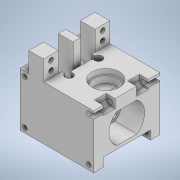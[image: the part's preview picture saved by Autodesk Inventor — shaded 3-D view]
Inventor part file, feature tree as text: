
AUTODESK INVENTOR PART (.ipt)
format: ipt  version: 2020 (Build 240168000, 168)  size: 453,120 bytes
history: native  units: mm
features: extrude x16, sketch x6, other x3
ambient origin geometry x8: Origin, YZ Plane, XZ Plane, XY Plane, X Axis, Y Axis, Z Axis, Center Point
bodies: Body1 (feature_tree)
feature tree (25):
  other  "Bryła1"
  extrude  "Wyciągnięcie proste1"  Depth=90.0mm
  sketch  "Szkic2"
  other  "Płaszczyzna konstrukcyjna1"
  extrude  "Wyciągnięcie proste2"  Depth=100.0mm
  extrude  "Wyciągnięcie proste3"  Depth=73.0mm TaperAngle=0.0deg
  sketch  "Szkic3"
  extrude  "Wyciągnięcie proste4"  Depth=6.5mm
  extrude  "Wyciągnięcie proste5"  Depth=6.5mm
  extrude  "Wyciągnięcie proste6"  Depth=6.5mm
  extrude  "Wyciągnięcie proste7"  Depth=6.5mm
  sketch  "Szkic4"
  extrude  "Wyciągnięcie proste8"  Depth=6.5mm
  extrude  "Wyciągnięcie proste9"  Depth=6.5mm
  extrude  "Wyciągnięcie proste10"  Depth=11.0mm
  extrude  "Wyciągnięcie proste11"  [1 undecoded]
  extrude  "Wyciągnięcie proste12"  Depth=64.0mm TaperAngle=0.0deg
  other  "Płaszczyzna konstrukcyjna2"
  extrude  "Wyciągnięcie proste13"  TaperAngle=0.0deg  [1 undecoded]
  extrude  "Wyciągnięcie proste14"  Depth=36.5mm
  extrude  "Wyciągnięcie proste15"  Depth=45.0mm
  extrude  "Wyciągnięcie proste16"  Depth=28.5mm
  sketch  "Szkic1"
  sketch  "Szkic5"
  sketch  "Szkic6"
note: 2 required parameter values undecoded (feature->parameter linkage not recoverable at this tier; creation-order binding heuristic only, values carry confidence <= 0.55)
